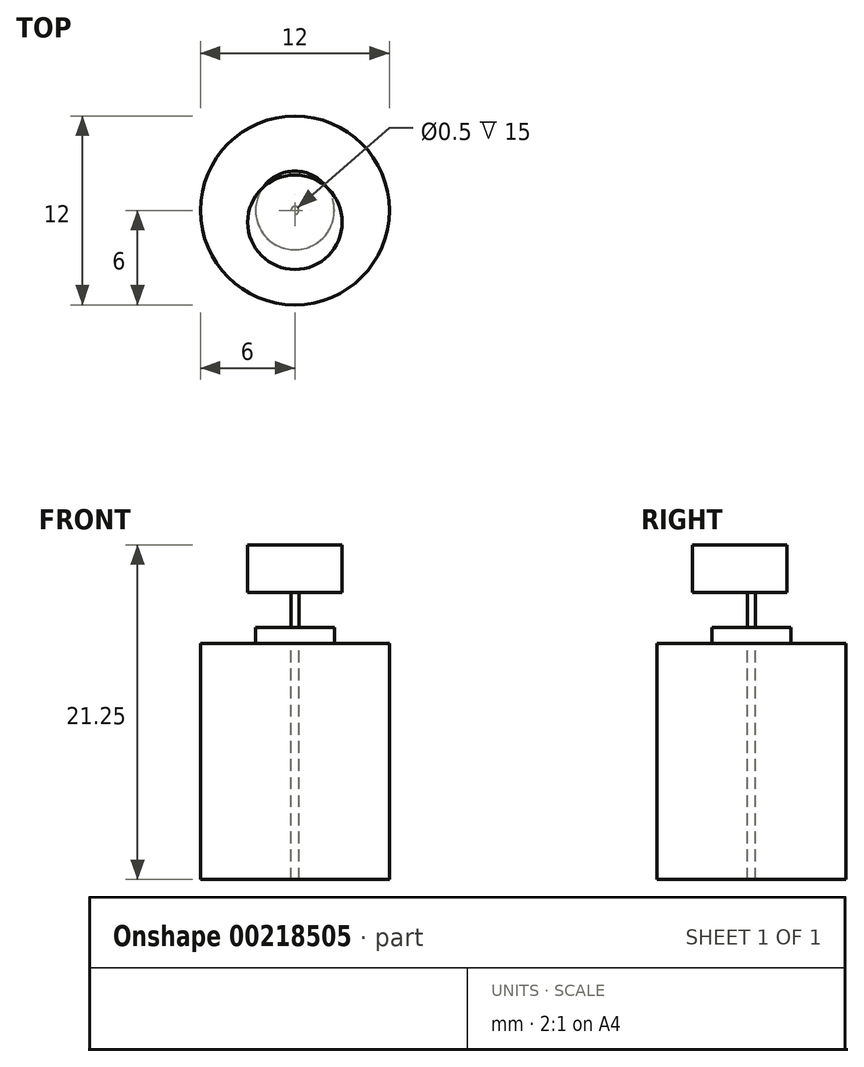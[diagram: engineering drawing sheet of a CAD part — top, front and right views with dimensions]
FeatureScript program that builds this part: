
annotation { "Feature Type Name" : "Feature", "Feature Type Description" : "" }
export const myFeature = defineFeature(function(context is Context, id is Id, definition is map)
    precondition{}
    {
        {
            var Q0;
            Q0=qCreatedBy(makeId("Top.planeOp"),FACE);
            var sketch = newSketch(context, id + "F0", { "sketchPlane" : qUnion([Q0])});
            skCircle(sketch, "E0", {"center": v(0, 0) * mm, "radius": 6 * mm});
            skCircle(sketch, "E1", {"center": v(0, 0) * mm, "radius": 2.5 * mm});
            skCircle(sketch, "E2", {"center": v(0, 0) * mm, "radius": 0.25 * mm});
            skSolve(sketch);
        }
        {
            var Q0;
            Q0=makeQuery(id+"F0.imprint","IMPRINT",FACE,{"disambiguationData":[TD([[makeQuery(id+"F0.imprint","IMPRINT",EDGE,{"derivedFrom":sQuery(id+"F0.wireOp",EDGE,"E0")}),1.0]])]});
            var Q1;
            Q1=makeQuery(id+"F0.imprint","IMPRINT",FACE,{"disambiguationData":[TD([[makeQuery(id+"F0.imprint","IMPRINT",EDGE,{"derivedFrom":sQuery(id+"F0.wireOp",EDGE,"E1")}),1.0]])]});
            extrude(context, id + "F1", {"entities" : qUnion([Q0, Q1]), "oppositeDirection" : true, "depth" : 15 * mm});
        }
        {
            var Q0;
            Q0=makeQuery(id+"F0.imprint","IMPRINT",FACE,{"disambiguationData":[TD([[makeQuery(id+"F0.imprint","IMPRINT",EDGE,{"derivedFrom":sQuery(id+"F0.wireOp",EDGE,"E1")}),1.0]])]});
            extrude(context, id + "F2", {"entities" : qUnion([Q0]), "operationType" : NewBodyOperationType.ADD, "depth" : 1 * mm});
        }
        {
            var Q0;
            Q0=makeQuery(id+"F0.imprint","IMPRINT",FACE,{"disambiguationData":[TD([[makeQuery(id+"F0.imprint","IMPRINT",EDGE,{"derivedFrom":sQuery(id+"F0.wireOp",EDGE,"E2")}),1.0]])]});
            extrude(context, id + "F3", {"entities" : qUnion([Q0]), "operationType" : NewBodyOperationType.ADD, "depth" : 6.25 * mm});
        }
        {
            var Q0;
            Q0=makeQuery(id+"F3.opExtrude","CAP_FACE",FACE,{"disambiguationData":[OSD([sQuery(id+"F0.wireOp",EDGE,"E2")])],"isStart":false});
            var sketch = newSketch(context, id + "F4", { "sketchPlane" : qUnion([Q0])});
            skCircle(sketch, "E3", {"center": v(0, -0.75) * mm, "radius": 3 * mm});
            skSolve(sketch);
        }
        {
            var Q0;
            Q0 = qSketchRegion(id + "F4", true);
            extrude(context, id + "F5", {"entities" : qUnion([Q0]), "operationType" : NewBodyOperationType.ADD, "oppositeDirection" : true, "depth" : 3 * mm});
        }
    });
